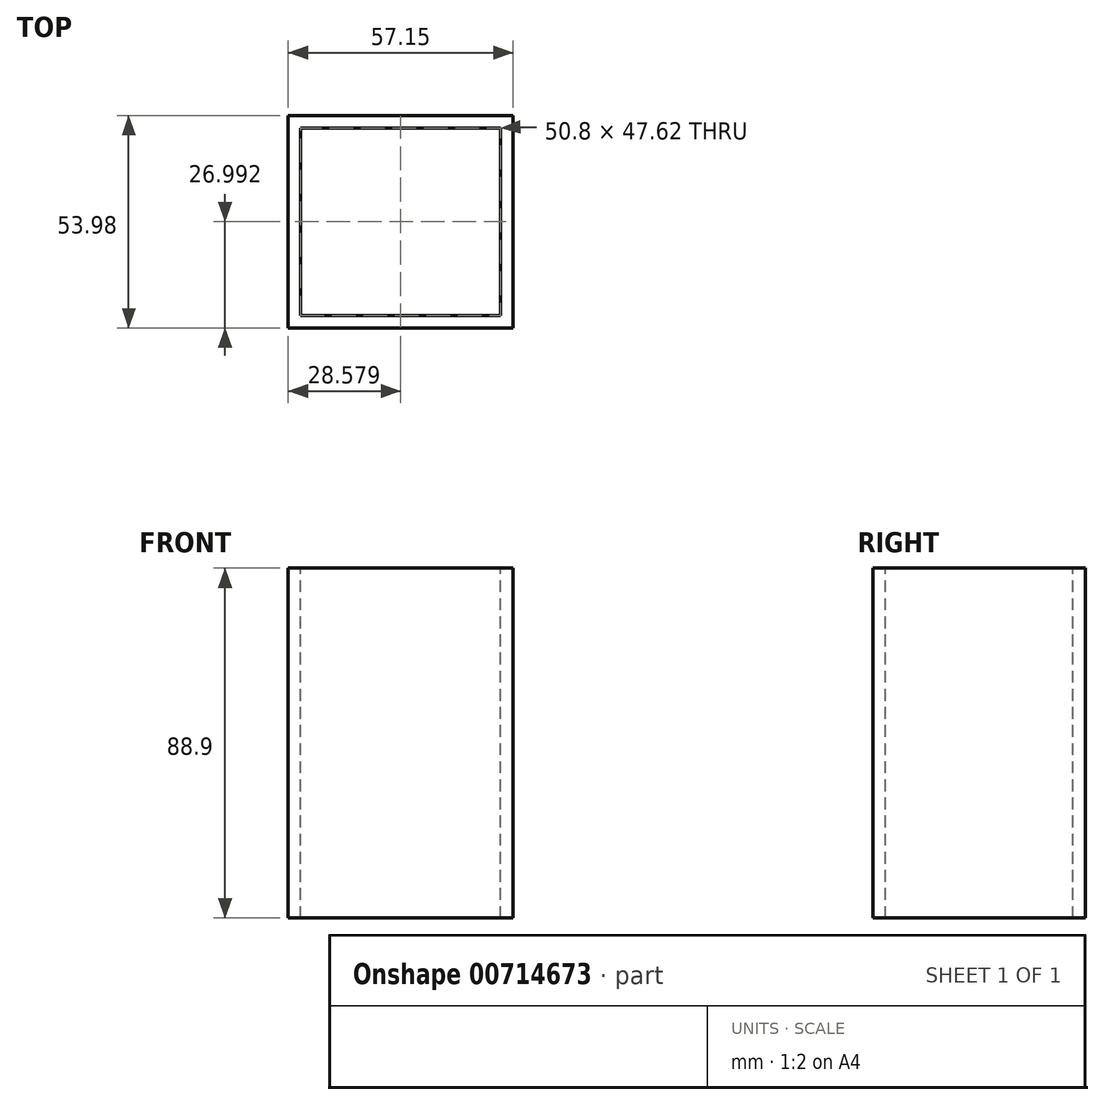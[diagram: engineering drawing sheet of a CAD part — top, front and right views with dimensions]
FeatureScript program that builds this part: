
annotation { "Feature Type Name" : "Feature", "Feature Type Description" : "" }
export const myFeature = defineFeature(function(context is Context, id is Id, definition is map)
    precondition{}
    {
        {
            var Q0;
            Q0=qCreatedBy(makeId("Front.planeOp"),FACE);
            var sketch = newSketch(context, id + "F0", { "sketchPlane" : qUnion([Q0])});
            skLineSegment(sketch, "E0.bottom", {"start": v(-32.98, 49.11) * mm, "end": v(24.17, 49.11) * mm});
            skLineSegment(sketch, "E0.top", {"start": v(-32.98, -39.79) * mm, "end": v(24.17, -39.79) * mm});
            skLineSegment(sketch, "E0.left", {"start": v(-32.98, 49.11) * mm, "end": v(-32.98, -39.79) * mm});
            skLineSegment(sketch, "E0.right", {"start": v(24.17, 49.11) * mm, "end": v(24.17, -39.79) * mm});
            skPoint(sketch, "E0.middle", {"position": v(-4.4, 4.66) * mm});
            skSolve(sketch);
        }
        {
            var Q0;
            Q0=makeQuery(id+"F0.imprint","IMPRINT",FACE,{"disambiguationData":[TD([[makeQuery(id+"F0.imprint","IMPRINT",EDGE,{"derivedFrom":sQuery(id+"F0.wireOp",EDGE,"E0.bottom")}),-1.0]])]});
            extrude(context, id + "F1", {"entities" : qUnion([Q0]), "depth" : 3.17 * mm, "offsetDistance" : 25.4 * mm});
        }
        {
            var Q0;
            Q0=makeQuery(id+"F1.opExtrude","CAP_FACE",FACE,{"disambiguationData":[OSD([sQuery(id+"F0.wireOp",EDGE,"E0.bottom"),sQuery(id+"F0.wireOp",EDGE,"E0.top"),sQuery(id+"F0.wireOp",EDGE,"E0.left"),sQuery(id+"F0.wireOp",EDGE,"E0.right")])],"isStart":false});
            var sketch = newSketch(context, id + "F2", { "sketchPlane" : qUnion([Q0])});
            skLineSegment(sketch, "E1.bottom", {"start": v(24.17, -39.79) * mm, "end": v(21, -39.79) * mm});
            skLineSegment(sketch, "E1.top", {"start": v(24.17, 49.11) * mm, "end": v(21, 49.11) * mm});
            skLineSegment(sketch, "E1.left", {"start": v(24.17, -39.79) * mm, "end": v(24.17, 49.11) * mm});
            skLineSegment(sketch, "E1.right", {"start": v(21, -39.79) * mm, "end": v(21, 49.11) * mm});
            skSolve(sketch);
        }
        {
            var Q0;
            Q0=makeQuery(id+"F2.imprint","IMPRINT",FACE,{"disambiguationData":[TD([[makeQuery(id+"F2.imprint","IMPRINT",EDGE,{"derivedFrom":sQuery(id+"F2.wireOp",EDGE,"E1.bottom")}),1.0]])]});
            extrude(context, id + "F3", {"entities" : qUnion([Q0]), "operationType" : NewBodyOperationType.ADD, "depth" : 50.8 * mm, "offsetDistance" : 25.4 * mm});
        }
        {
            var Q0;
            Q0=makeQuery(id+"F1.opExtrude","CAP_FACE",FACE,{"disambiguationData":[OSD([sQuery(id+"F0.wireOp",EDGE,"E0.bottom"),sQuery(id+"F0.wireOp",EDGE,"E0.top"),sQuery(id+"F0.wireOp",EDGE,"E0.left"),sQuery(id+"F0.wireOp",EDGE,"E0.right")])],"isStart":false});
            var sketch = newSketch(context, id + "F4", { "sketchPlane" : qUnion([Q0])});
            skLineSegment(sketch, "E2.bottom", {"start": v(-32.98, -39.79) * mm, "end": v(-29.8, -39.79) * mm});
            skLineSegment(sketch, "E2.top", {"start": v(-32.98, 49.11) * mm, "end": v(-29.8, 49.11) * mm});
            skLineSegment(sketch, "E2.left", {"start": v(-32.98, -39.79) * mm, "end": v(-32.98, 49.11) * mm});
            skLineSegment(sketch, "E2.right", {"start": v(-29.8, -39.79) * mm, "end": v(-29.8, 49.11) * mm});
            skSolve(sketch);
        }
        {
            var Q0;
            Q0=makeQuery(id+"F4.imprint","IMPRINT",FACE,{"disambiguationData":[TD([[makeQuery(id+"F4.imprint","IMPRINT",EDGE,{"derivedFrom":sQuery(id+"F4.wireOp",EDGE,"E2.bottom")}),1.0]])]});
            extrude(context, id + "F5", {"entities" : qUnion([Q0]), "operationType" : NewBodyOperationType.ADD, "depth" : 50.8 * mm, "offsetDistance" : 25.4 * mm});
        }
        {
            var Q0;
            Q0=makeQuery(id+"F5.opExtrude","SWEPT_FACE",FACE,{"disambiguationData":[OSD([sQuery(id+"F4.wireOp",EDGE,"E2.right")])]});
            var sketch = newSketch(context, id + "F6", { "sketchPlane" : qUnion([Q0])});
            skLineSegment(sketch, "E3.bottom", {"start": v(-53.98, -39.79) * mm, "end": v(-50.8, -39.79) * mm});
            skLineSegment(sketch, "E3.top", {"start": v(-53.98, 49.11) * mm, "end": v(-50.8, 49.11) * mm});
            skLineSegment(sketch, "E3.left", {"start": v(-53.98, -39.79) * mm, "end": v(-53.98, 49.11) * mm});
            skLineSegment(sketch, "E3.right", {"start": v(-50.8, -39.79) * mm, "end": v(-50.8, 49.11) * mm});
            skSolve(sketch);
        }
        {
            var Q0;
            Q0=makeQuery(id+"F6.imprint","IMPRINT",FACE,{"disambiguationData":[TD([[makeQuery(id+"F6.imprint","IMPRINT",EDGE,{"derivedFrom":sQuery(id+"F6.wireOp",EDGE,"E3.bottom")}),1.0]])]});
            extrude(context, id + "F7", {"entities" : qUnion([Q0]), "operationType" : NewBodyOperationType.ADD, "depth" : 50.8 * mm, "offsetDistance" : 25.4 * mm});
        }
    });
